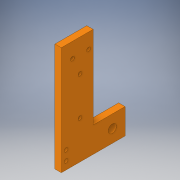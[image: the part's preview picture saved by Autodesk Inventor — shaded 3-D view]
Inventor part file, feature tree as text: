
AUTODESK INVENTOR PART (.ipt)
format: ipt  version: 2019 (Build 230136000, 136)  size: 150,016 bytes
history: native  units: in
note: dims shown in document units (in); Inventor stores cm internally (conversion verified against a paired STEP export)
features: sketch x6, hole x4, extrude x2, projected_geometry x2
ambient origin geometry x8: Origin, YZ Plane, XZ Plane, XY Plane, X Axis, Y Axis, Z Axis, Center Point
bodies: Solid1 (feature_tree)
feature tree (14):
  extrude  "Extrusion1"  Depth=2.25in
  hole  "Hole1"  [1 undecoded]
  hole  "Hole2"  [1 undecoded]
  hole  "Hole3"  [1 undecoded]
  extrude  "Extrusion2"  Depth=1.0in
  hole  "Hole4"  [1 undecoded]
  sketch  "Sketch1"  dims[d0=4.25in d1=2.25in]
  sketch  "Sketch2"  dims[d2=3.25in d3=1.25in]
  projected_geometry  "Projected Loop1"
  sketch  "Sketch3"  dims[d4=0.25in d5=0.0in d6=3.661in]
  sketch  "Sketch4"  dims[d7=3.661in d8=0.63in]
  sketch  "Sketch5"  dims[d9=1.0in d10=0.185in]
  projected_geometry  "Projected Loop2"
  sketch  "Sketch6"  dims[d11=0.15in d12=0.75in d13=0.375in d14=0.25in d15=0.5635in d16=1.0in d17=0.8108in d18=0.5in d19=0.5in d20=0.32in d21=0.75in d22=0.375in d23=0.25in d24=0.5635in d25=1.0in d26=0.8108in d29=1.5in d30=3.0in d31=0.15in d32=0.75in d33=0.375in d34=0.25in d35=0.5635in d36=0.432in d37=0.8108in d38=0.522in d39=0.522in d40=0.25in d41=0.0in d42=0.1875in d43=0.1875in d44=0.375in d45=0.3125in d46=0.15in d47=0.75in d48=0.375in d49=0.25in d50=0.5635in d51=0.432in d52=0.8108in]
note: 4 required parameter values undecoded (feature->parameter linkage not recoverable at this tier; creation-order binding heuristic only, values carry confidence <= 0.55)
